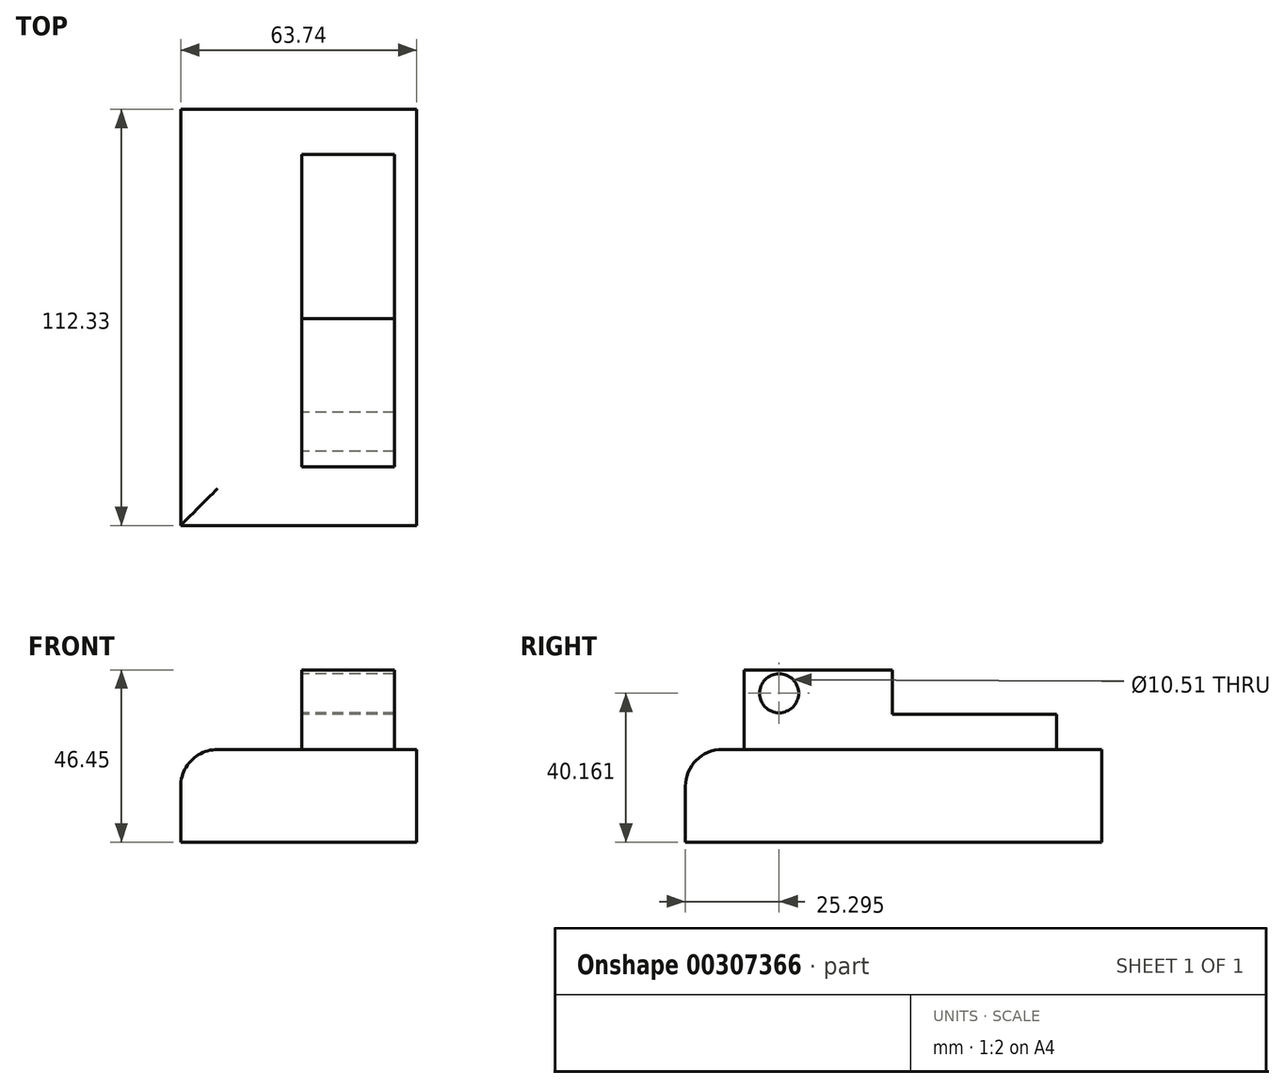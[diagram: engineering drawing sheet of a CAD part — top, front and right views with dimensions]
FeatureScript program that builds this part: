
annotation { "Feature Type Name" : "Feature", "Feature Type Description" : "" }
export const myFeature = defineFeature(function(context is Context, id is Id, definition is map)
    precondition{}
    {
        {
            var Q0;
            Q0=qCreatedBy(makeId("Top.planeOp"),FACE);
            var sketch = newSketch(context, id + "F0", { "sketchPlane" : qUnion([Q0])});
            skLineSegment(sketch, "E0.bottom", {"start": v(-32.73, 56.45) * mm, "end": v(31.01, 56.45) * mm});
            skLineSegment(sketch, "E0.top", {"start": v(-32.73, -55.88) * mm, "end": v(31.01, -55.88) * mm});
            skLineSegment(sketch, "E0.left", {"start": v(-32.73, 56.45) * mm, "end": v(-32.73, -55.88) * mm});
            skLineSegment(sketch, "E0.right", {"start": v(31.01, 56.45) * mm, "end": v(31.01, -55.88) * mm});
            skLineSegment(sketch, "E1.bottom", {"start": v(-9, 50.45) * mm, "end": v(8.15, 50.45) * mm});
            skLineSegment(sketch, "E1.top", {"start": v(-9, -50.17) * mm, "end": v(8.15, -50.17) * mm});
            skLineSegment(sketch, "E1.left", {"start": v(-9, 50.45) * mm, "end": v(-9, -50.17) * mm});
            skLineSegment(sketch, "E1.right", {"start": v(8.15, 50.45) * mm, "end": v(8.15, -50.17) * mm});
            skSolve(sketch);
        }
        {
            var Q0;
            Q0=makeQuery(id+"F0.imprint","IMPRINT",FACE,{"disambiguationData":[TD([[makeQuery(id+"F0.imprint","IMPRINT",EDGE,{"derivedFrom":sQuery(id+"F0.wireOp",EDGE,"E1.bottom")}),-1.0]])]});
            var Q1;
            Q1=makeQuery(id+"F0.imprint","IMPRINT",FACE,{"disambiguationData":[TD([[makeQuery(id+"F0.imprint","IMPRINT",EDGE,{"derivedFrom":sQuery(id+"F0.wireOp",EDGE,"E0.bottom")}),-1.0]])]});
            extrude(context, id + "F1", {"entities" : qUnion([Q0, Q1]), "depth" : 25 * mm});
        }
        {
            var Q0;
            Q0=qCreatedBy(makeId("Right.planeOp"),FACE);
            var sketch = newSketch(context, id + "F2", { "sketchPlane" : qUnion([Q0])});
            skLineSegment(sketch, "E2.bottom", {"start": v(-40.02, 25.01) * mm, "end": v(44.3, 25.01) * mm});
            skLineSegment(sketch, "E2.top", {"start": v(-40.02, 46.45) * mm, "end": v(44.3, 46.45) * mm});
            skLineSegment(sketch, "E2.left", {"start": v(-40.02, 25.01) * mm, "end": v(-40.02, 46.45) * mm});
            skLineSegment(sketch, "E2.right", {"start": v(44.3, 25.01) * mm, "end": v(44.3, 46.45) * mm});
            skCircle(sketch, "E3", {"center": v(-30.59, 40.16) * mm, "radius": 5.26 * mm});
            skLineSegment(sketch, "E4.bottom", {"start": v(44.3, 46.45) * mm, "end": v(0, 46.45) * mm});
            skLineSegment(sketch, "E4.top", {"start": v(44.3, 34.44) * mm, "end": v(0, 34.44) * mm});
            skLineSegment(sketch, "E4.left", {"start": v(44.3, 46.45) * mm, "end": v(44.3, 34.44) * mm});
            skLineSegment(sketch, "E4.right", {"start": v(0, 46.45) * mm, "end": v(0, 34.44) * mm});
            skSolve(sketch);
        }
        {
            var Q0;
            Q0=makeQuery(id+"F2.imprint","IMPRINT",FACE,{"disambiguationData":[TD([[makeQuery(id+"F2.imprint","IMPRINT",EDGE,{"derivedFrom":sQuery(id+"F2.wireOp",EDGE,"E2.bottom")}),1.0]])]});
            extrude(context, id + "F3", {"entities" : qUnion([Q0]), "depth" : 25 * mm});
        }
        {
            var Q0;
            Q0=makeQuery(id+"F1.opExtrude","CAP_EDGE",EDGE,{"disambiguationData":[OSD([sQuery(id+"F0.wireOp",EDGE,"E0.left")])],"isStart":false});
            var Q1;
            Q1=makeQuery(id+"F1.opExtrude","CAP_EDGE",EDGE,{"disambiguationData":[OSD([sQuery(id+"F0.wireOp",EDGE,"E0.top")])],"isStart":false});
            fillet(context, id + "F4", {"entities" : qUnion([Q0, Q1]), "radius" : 10 * mm, "tangentPropagation" : true, "allowEdgeOverflow" : false});
        }
    });
